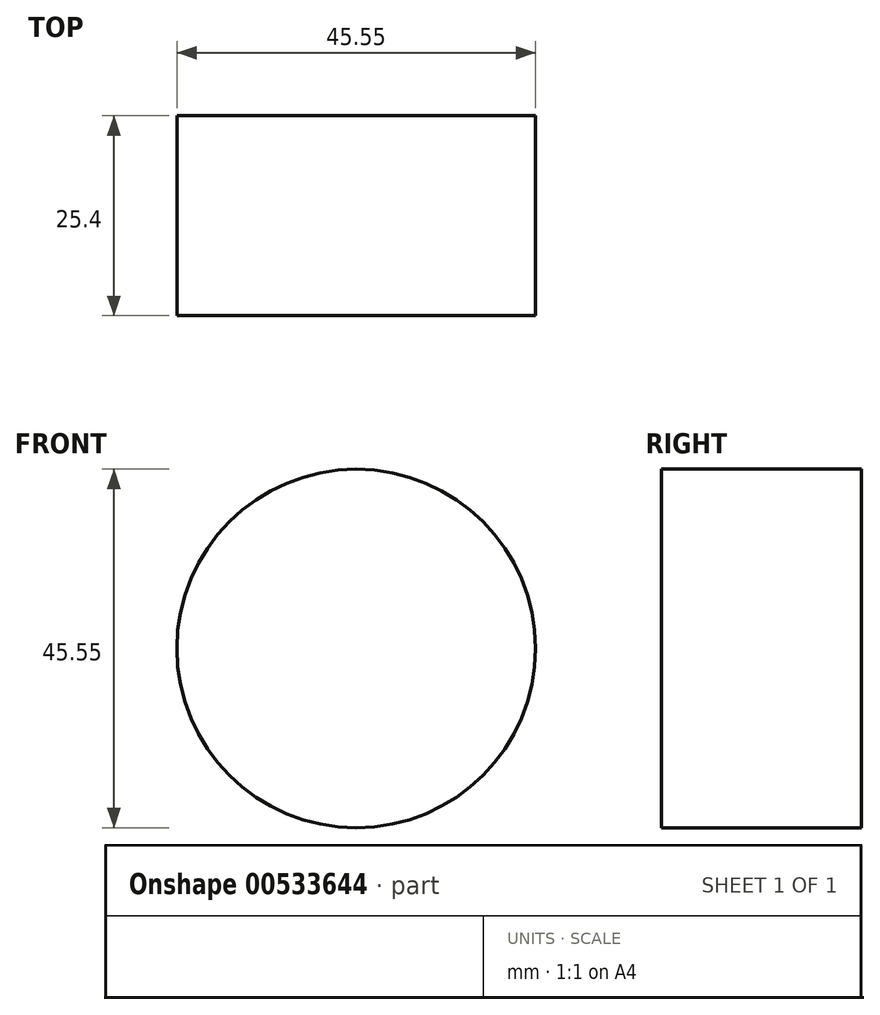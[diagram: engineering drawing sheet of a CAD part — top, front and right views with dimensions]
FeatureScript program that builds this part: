
annotation { "Feature Type Name" : "Feature", "Feature Type Description" : "" }
export const myFeature = defineFeature(function(context is Context, id is Id, definition is map)
    precondition{}
    {
        {
            var Q0;
            Q0=qCreatedBy(makeId("Front.planeOp"),FACE);
            var sketch = newSketch(context, id + "F0", { "sketchPlane" : qUnion([Q0])});
            skCircle(sketch, "E0", {"center": v(-51.47, 32.73) * mm, "radius": 22.78 * mm});
            skSolve(sketch);
        }
        {
            var Q0;
            Q0=makeQuery(id+"F0.imprint","IMPRINT",FACE,{"disambiguationData":[TD([[makeQuery(id+"F0.imprint","IMPRINT",EDGE,{"derivedFrom":sQuery(id+"F0.wireOp",EDGE,"E0")}),1.0]])]});
            extrude(context, id + "F1", {"entities" : qUnion([Q0]), "depth" : 25.4 * mm, "offsetDistance" : 25.4 * mm});
        }
    });
